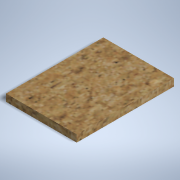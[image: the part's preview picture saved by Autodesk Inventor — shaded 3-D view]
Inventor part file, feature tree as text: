
AUTODESK INVENTOR PART (.ipt)
format: ipt  version: 2022 (Build 260153000, 153)  size: 260,096 bytes
history: native  units: mm
features: extrude x1, sketch x1
ambient origin geometry x8: Origin, YZ Plane, XZ Plane, XY Plane, X Axis, Y Axis, Z Axis, Center Point
bodies: Body1 (feature_tree)
feature tree (2):
  extrude  "Выдавливание2"  Depth=235.0mm
  sketch  "Эскиз3"
